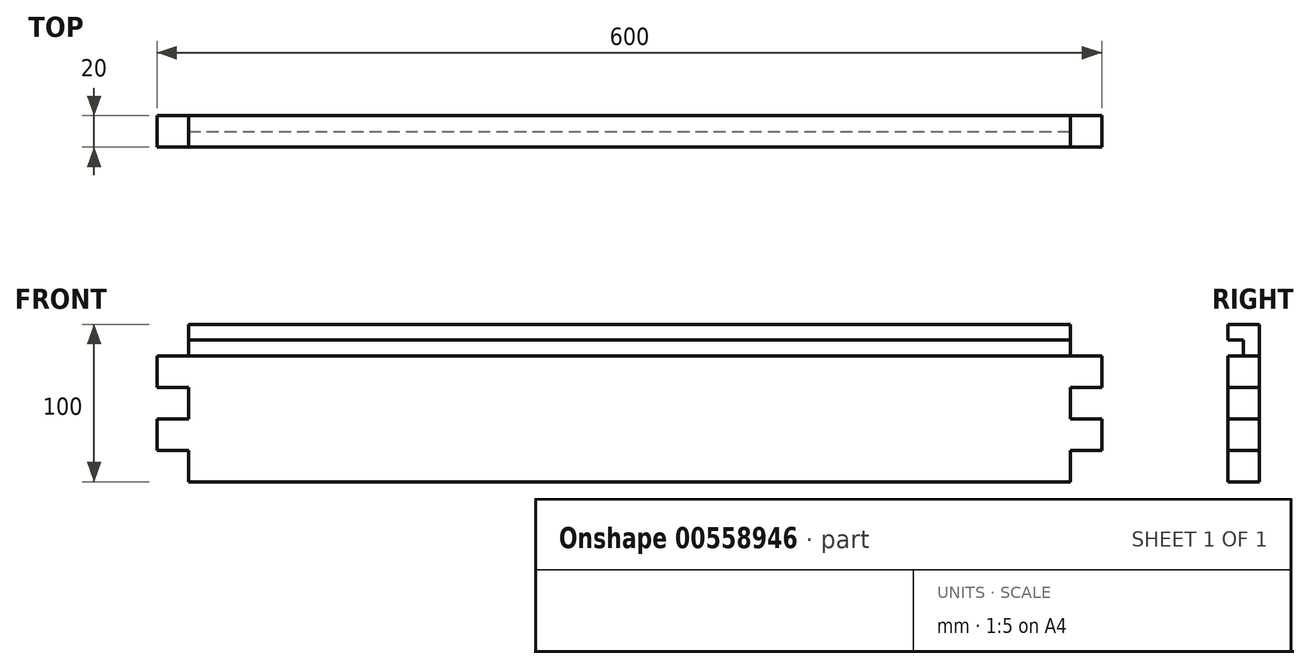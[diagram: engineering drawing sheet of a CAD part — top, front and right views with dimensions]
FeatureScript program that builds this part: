
annotation { "Feature Type Name" : "Feature", "Feature Type Description" : "" }
export const myFeature = defineFeature(function(context is Context, id is Id, definition is map)
    precondition{}
    {
        {
            var Q0;
            Q0=qCreatedBy(makeId("Front.planeOp"),FACE);
            var sketch = newSketch(context, id + "F0", { "sketchPlane" : qUnion([Q0])});
            skLineSegment(sketch, "E0.bottom", {"start": v(300, -50) * mm, "end": v(-300, -50) * mm});
            skLineSegment(sketch, "E0.top", {"start": v(300, 50) * mm, "end": v(-300, 50) * mm});
            skLineSegment(sketch, "E0.left", {"start": v(300, -50) * mm, "end": v(300, 50) * mm});
            skLineSegment(sketch, "E0.right", {"start": v(-300, -50) * mm, "end": v(-300, 50) * mm});
            skPoint(sketch, "E0.middle", {"position": v(0, 0) * mm});
            skSolve(sketch);
        }
        {
            var Q0;
            Q0=makeQuery(id+"F0.imprint","IMPRINT",FACE,{"disambiguationData":[TD([[makeQuery(id+"F0.imprint","IMPRINT",EDGE,{"derivedFrom":sQuery(id+"F0.wireOp",EDGE,"E0.bottom")}),-1.0]])]});
            extrude(context, id + "F1", {"entities" : qUnion([Q0]), "depth" : 20 * mm, "offsetDistance" : 25 * mm});
        }
        {
            var Q0;
            Q0=makeQuery(id+"F1.opExtrude","CAP_FACE",FACE,{"disambiguationData":[OSD([sQuery(id+"F0.wireOp",EDGE,"E0.bottom"),sQuery(id+"F0.wireOp",EDGE,"E0.top"),sQuery(id+"F0.wireOp",EDGE,"E0.left"),sQuery(id+"F0.wireOp",EDGE,"E0.right")])],"isStart":true});
            var sketch = newSketch(context, id + "F2", { "sketchPlane" : qUnion([Q0])});
            skLineSegment(sketch, "E1.bottom", {"start": v(-300, -50) * mm, "end": v(-280, -50) * mm});
            skLineSegment(sketch, "E1.top", {"start": v(-300, -30) * mm, "end": v(-280, -30) * mm});
            skLineSegment(sketch, "E1.left", {"start": v(-300, -50) * mm, "end": v(-300, -30) * mm});
            skLineSegment(sketch, "E1.right", {"start": v(-280, -50) * mm, "end": v(-280, -30) * mm});
            skLineSegment(sketch, "E2.bottom", {"start": v(-300, -10) * mm, "end": v(-280, -10) * mm});
            skLineSegment(sketch, "E2.top", {"start": v(-300, 10) * mm, "end": v(-280, 10) * mm});
            skLineSegment(sketch, "E2.left", {"start": v(-300, -10) * mm, "end": v(-300, 10) * mm});
            skLineSegment(sketch, "E2.right", {"start": v(-280, -10) * mm, "end": v(-280, 10) * mm});
            skLineSegment(sketch, "E3.MirrorCS", {"start": v(300, -10) * mm, "end": v(300, 10) * mm});
            skLineSegment(sketch, "E4.MirrorCS", {"start": v(300, 10) * mm, "end": v(280, 10) * mm});
            skLineSegment(sketch, "E5.MirrorCS", {"start": v(300, -10) * mm, "end": v(280, -10) * mm});
            skLineSegment(sketch, "E6.MirrorCS", {"start": v(280, -50) * mm, "end": v(280, -30) * mm});
            skLineSegment(sketch, "E7.MirrorCS", {"start": v(300, -50) * mm, "end": v(300, -30) * mm});
            skLineSegment(sketch, "E8.MirrorCS", {"start": v(300, -30) * mm, "end": v(280, -30) * mm});
            skLineSegment(sketch, "E9.MirrorCS", {"start": v(280, -10) * mm, "end": v(280, 10) * mm});
            skLineSegment(sketch, "E10.MirrorCS", {"start": v(300, -50) * mm, "end": v(280, -50) * mm});
            skLineSegment(sketch, "E11.bottom", {"start": v(300, 30) * mm, "end": v(280, 30) * mm});
            skLineSegment(sketch, "E11.top", {"start": v(300, 50) * mm, "end": v(280, 50) * mm});
            skLineSegment(sketch, "E11.left", {"start": v(300, 30) * mm, "end": v(300, 50) * mm});
            skLineSegment(sketch, "E11.right", {"start": v(280, 30) * mm, "end": v(280, 50) * mm});
            skLineSegment(sketch, "E12.MirrorCS", {"start": v(-300, 30) * mm, "end": v(-280, 30) * mm});
            skLineSegment(sketch, "E13.MirrorCS", {"start": v(-300, 30) * mm, "end": v(-300, 50) * mm});
            skLineSegment(sketch, "E14.MirrorCS", {"start": v(-300, 50) * mm, "end": v(-280, 50) * mm});
            skLineSegment(sketch, "E15.MirrorCS", {"start": v(-280, 30) * mm, "end": v(-280, 50) * mm});
            skSolve(sketch);
        }
        {
            var Q0;
            Q0=qSketchRegion(id+"F2",true);
            extrude(context, id + "F3", {"entities" : qUnion([Q0]), "operationType" : NewBodyOperationType.REMOVE, "endBound" : BoundingType.UP_TO_NEXT, "oppositeDirection" : true, "depth" : 25 * mm, "offsetDistance" : 25 * mm});
        }
        {
            var Q0;
            Q0=makeQuery(id+"F1.opExtrude","CAP_FACE",FACE,{"disambiguationData":[OSD([sQuery(id+"F0.wireOp",EDGE,"E0.bottom"),sQuery(id+"F0.wireOp",EDGE,"E0.top"),sQuery(id+"F0.wireOp",EDGE,"E0.left"),sQuery(id+"F0.wireOp",EDGE,"E0.right")])],"isStart":false});
            var sketch = newSketch(context, id + "F4", { "sketchPlane" : qUnion([Q0])});
            skLineSegment(sketch, "E16.bottom", {"start": v(300, 30) * mm, "end": v(-300, 30) * mm});
            skLineSegment(sketch, "E16.top", {"start": v(300, 40) * mm, "end": v(-300, 40) * mm});
            skLineSegment(sketch, "E16.left", {"start": v(300, 30) * mm, "end": v(300, 40) * mm});
            skLineSegment(sketch, "E16.right", {"start": v(-300, 30) * mm, "end": v(-300, 40) * mm});
            skPoint(sketch, "E16.middle", {"position": v(0, 35) * mm});
            skSolve(sketch);
        }
        {
            var Q0;
            Q0 = qSketchRegion(id + "F4", true);
            extrude(context, id + "F5", {"entities" : qUnion([Q0]), "operationType" : NewBodyOperationType.REMOVE, "oppositeDirection" : true, "depth" : 10 * mm, "offsetDistance" : 25 * mm});
        }
    });
